# Revit family: Toilet_Seat-Elongated_Closed_Front-KALLISTA-Ultra-P78634
name_source: partatom
category: Specialty Equipment
units: mm (PartAtom-declared; Revit-internal decimal feet)

## family parameters
Cut with Voids When Loaded = No
Host = Face
Maintain Annotation Orientation = No
OmniClass Number = 23.31.19.19.17
Part Type = Normal
Room Calculation Point = No
Round Connector Dimension = Use Diameter
Shared = No

## types (1)
- 0-White
    ADA Compliant = No
    Assembly Code = C1030200
    Date Modified = 08/21/2025
    Default Elevation = 15"
    Description = Ultra-thin toilet seat
    Finish = Kallista-Plastic-0-White
    Height = 2"
    Length = 19 3/8"
    Manufacturer = Kallista Co.
    Master Format 2014 = 10 28 00
    Master Format 2014 Name = Toilet, Bath, and Laundry Accessories
    Material = Plastic Construction
    Model = P78634-00-0
    Product Documentation Link = https://techcomm.kohler.com
    Product Name = Ultra
    Product Page URL = https://www.kallista.com
    Type = 1
    URL = https://www.kallista.com
    WaterSense Certified = No
    Width = 14 3/8"

## geometry (parser evidence)
native form markers: Sweep x7
no freeform markers — native parametric forms only
